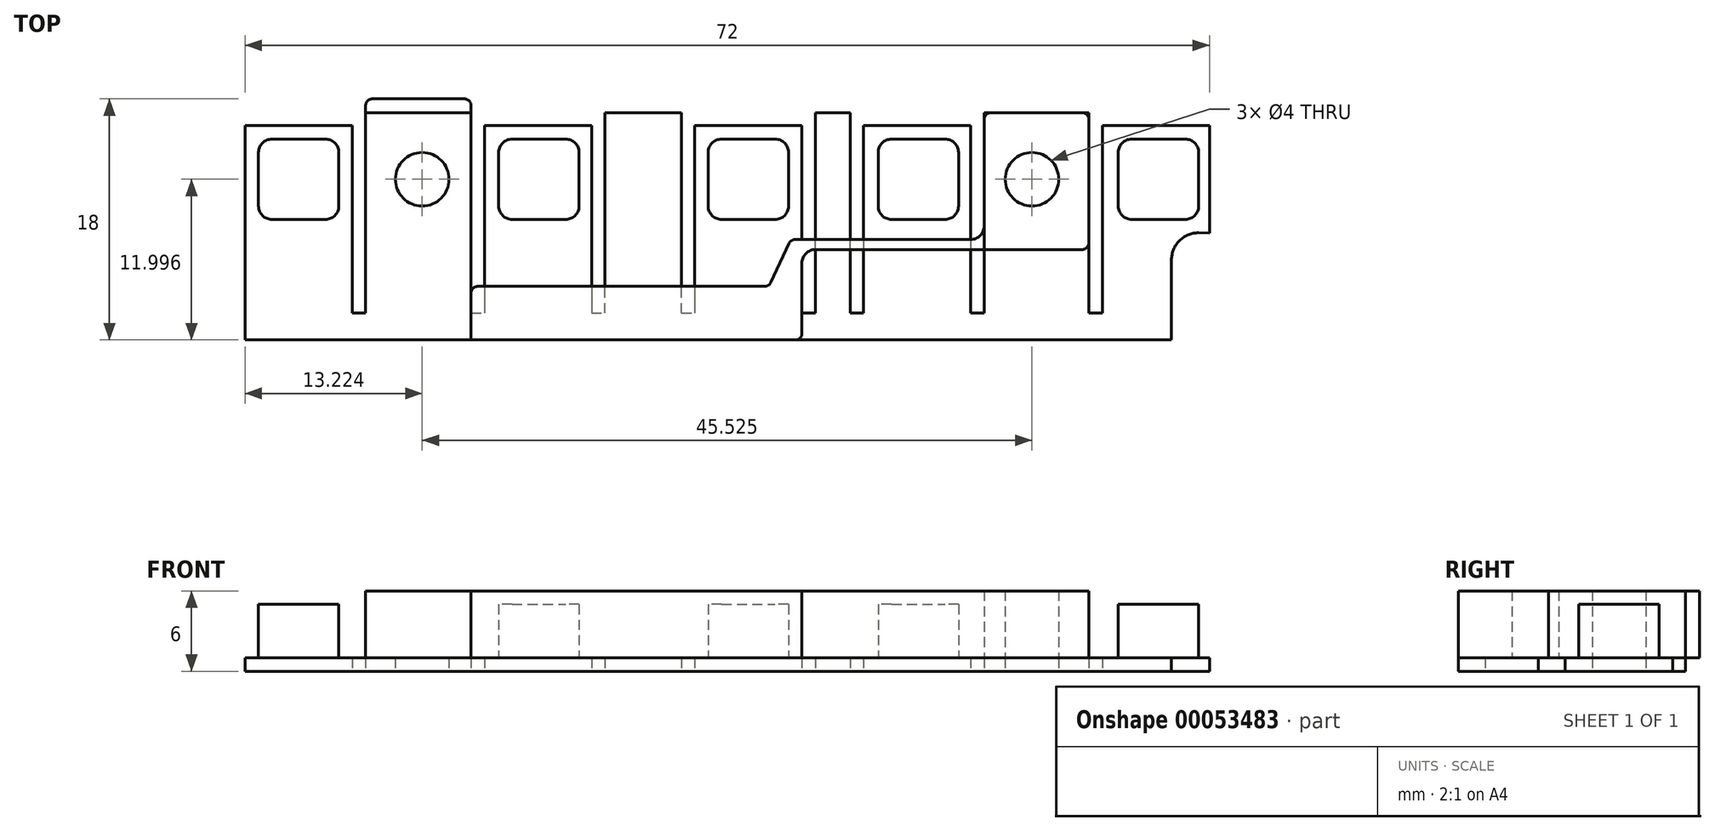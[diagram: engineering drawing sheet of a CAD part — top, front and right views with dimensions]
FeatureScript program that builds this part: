
annotation { "Feature Type Name" : "Feature", "Feature Type Description" : "" }
export const myFeature = defineFeature(function(context is Context, id is Id, definition is map)
    precondition{}
    {
        {
            var Q0;
            Q0=qCreatedBy(makeId("Top.planeOp"),FACE);
            var sketch = newSketch(context, id + "F0", { "sketchPlane" : qUnion([Q0])});
            skLineSegment(sketch, "E0.bottom", {"start": v(-36.4, 9.03) * mm, "end": v(39.6, 9.03) * mm});
            skLineSegment(sketch, "E0.top", {"start": v(-36.4, -6.97) * mm, "end": v(39.6, -6.97) * mm});
            skLineSegment(sketch, "E0.left", {"start": v(-36.4, 9.03) * mm, "end": v(-36.4, -6.97) * mm});
            skLineSegment(sketch, "E0.right", {"start": v(39.6, 9.03) * mm, "end": v(39.6, -6.97) * mm});
            skLineSegment(sketch, "E1", {"start": v(-30.3, 13.5) * mm, "end": v(-30.3, -12.05) * mm, "construction": true});
            skLineSegment(sketch, "E2.1.0.0", {"start": v(-21.08, 13.58) * mm, "end": v(-21.08, -11.98) * mm, "construction": true});
            skLineSegment(sketch, "E2.2.0.0", {"start": v(3.27, 13.5) * mm, "end": v(3.27, -12.05) * mm, "construction": true});
            skLineSegment(sketch, "E2.3.0.0", {"start": v(24.45, 13.5) * mm, "end": v(24.45, -12.05) * mm, "construction": true});
            skLineSegment(sketch, "E2.4.0.0", {"start": v(33.7, 13.5) * mm, "end": v(33.7, -12.05) * mm, "construction": true});
            skLineSegment(sketch, "E2.5.0.0", {"start": v(15.87, 13.5) * mm, "end": v(15.87, -12.05) * mm, "construction": true});
            skLineSegment(sketch, "E2.6.0.0", {"start": v(-12.43, 13.5) * mm, "end": v(-12.43, -12.05) * mm, "construction": true});
            skLineSegment(sketch, "E3", {"start": v(-40.05, 5.03) * mm, "end": v(48.02, 5.03) * mm, "construction": true});
            skCircle(sketch, "E4", {"center": v(-21.08, 5.03) * mm, "radius": 2 * mm});
            skCircle(sketch, "E5", {"center": v(24.45, 5.03) * mm, "radius": 2 * mm});
            skLineSegment(sketch, "E6.rect.bottom", {"start": v(-33.3, 8.03) * mm, "end": v(-27.3, 8.03) * mm});
            skLineSegment(sketch, "E6.rect.top", {"start": v(-33.3, 2.03) * mm, "end": v(-27.3, 2.03) * mm});
            skLineSegment(sketch, "E6.rect.left", {"start": v(-33.3, 8.03) * mm, "end": v(-33.3, 2.03) * mm});
            skLineSegment(sketch, "E6.rect.right", {"start": v(-27.3, 8.03) * mm, "end": v(-27.3, 2.03) * mm});
            skPoint(sketch, "E6.rect.middle", {"position": v(-30.3, 5.03) * mm});
            skLineSegment(sketch, "E7.rect.left", {"start": v(-15.36, 8.03) * mm, "end": v(-15.36, 2.03) * mm});
            skLineSegment(sketch, "E7.rect.bottom", {"start": v(-15.36, 8.03) * mm, "end": v(-9.36, 8.03) * mm});
            skLineSegment(sketch, "E7.rect.right", {"start": v(-9.36, 8.03) * mm, "end": v(-9.36, 2.03) * mm});
            skLineSegment(sketch, "E7.rect.top", {"start": v(-15.36, 2.03) * mm, "end": v(-9.36, 2.03) * mm});
            skLineSegment(sketch, "E8.rect.left", {"start": v(0.27, 8.03) * mm, "end": v(0.27, 2.03) * mm});
            skLineSegment(sketch, "E8.rect.bottom", {"start": v(0.27, 8.03) * mm, "end": v(6.27, 8.03) * mm});
            skLineSegment(sketch, "E8.rect.right", {"start": v(6.27, 8.03) * mm, "end": v(6.27, 2.03) * mm});
            skLineSegment(sketch, "E8.rect.top", {"start": v(0.27, 2.03) * mm, "end": v(6.27, 2.03) * mm});
            skLineSegment(sketch, "E9.rect.left", {"start": v(12.96, 8.03) * mm, "end": v(12.96, 2.03) * mm});
            skLineSegment(sketch, "E9.rect.bottom", {"start": v(12.96, 8.03) * mm, "end": v(18.96, 8.03) * mm});
            skLineSegment(sketch, "E9.rect.right", {"start": v(18.96, 8.03) * mm, "end": v(18.96, 2.03) * mm});
            skLineSegment(sketch, "E9.rect.top", {"start": v(12.96, 2.03) * mm, "end": v(18.96, 2.03) * mm});
            skLineSegment(sketch, "E10.rect.left", {"start": v(30.9, 8.03) * mm, "end": v(30.9, 2.03) * mm});
            skLineSegment(sketch, "E10.rect.bottom", {"start": v(30.9, 8.03) * mm, "end": v(36.9, 8.03) * mm});
            skLineSegment(sketch, "E10.rect.right", {"start": v(36.9, 8.03) * mm, "end": v(36.9, 2.03) * mm});
            skLineSegment(sketch, "E10.rect.top", {"start": v(30.9, 2.03) * mm, "end": v(36.9, 2.03) * mm});
            skLineSegment(sketch, "E11", {"start": v(-41.7, 2.03) * mm, "end": v(44.73, 2.03) * mm, "construction": true});
            skLineSegment(sketch, "E12", {"start": v(-41.7, -4.97) * mm, "end": v(44.73, -4.97) * mm, "construction": true});
            skLineSegment(sketch, "E13.top", {"start": v(-36.4, 11.03) * mm, "end": v(39.58, 11.03) * mm});
            skLineSegment(sketch, "E13.left", {"start": v(-36.4, 9.03) * mm, "end": v(-36.4, 11.03) * mm});
            skLineSegment(sketch, "E13.right", {"start": v(39.58, 8.03) * mm, "end": v(39.58, 11.03) * mm});
            skLineSegment(sketch, "E14.bottom", {"start": v(-34.3, 9.03) * mm, "end": v(-26.3, 9.03) * mm});
            skLineSegment(sketch, "E14.left", {"start": v(-34.3, 9.03) * mm, "end": v(-34.3, -4.97) * mm});
            skLineSegment(sketch, "E14.right", {"start": v(-26.3, 9.03) * mm, "end": v(-26.3, -4.97) * mm});
            skLineSegment(sketch, "E15.bottom", {"start": v(-26.3, -4.97) * mm, "end": v(-36.4, -4.97) * mm});
            skLineSegment(sketch, "E15.right", {"start": v(-36.4, -4.97) * mm, "end": v(-36.4, 9.03) * mm});
            skLineSegment(sketch, "E16.bottom", {"start": v(-35.3, -4.97) * mm, "end": v(-25.3, -4.97) * mm});
            skLineSegment(sketch, "E16.top", {"start": v(-35.3, 9.03) * mm, "end": v(-25.3, 9.03) * mm});
            skLineSegment(sketch, "E16.left", {"start": v(-35.3, -4.97) * mm, "end": v(-35.3, 9.03) * mm});
            skLineSegment(sketch, "E16.right", {"start": v(-25.3, -4.97) * mm, "end": v(-25.3, 9.03) * mm});
            skLineSegment(sketch, "E17.right", {"start": v(-7.43, -4.97) * mm, "end": v(-7.43, 9.03) * mm});
            skLineSegment(sketch, "E17.top", {"start": v(-17.43, 9.03) * mm, "end": v(-7.43, 9.03) * mm});
            skLineSegment(sketch, "E17.left", {"start": v(-17.43, -4.97) * mm, "end": v(-17.43, 9.03) * mm});
            skLineSegment(sketch, "E17.bottom", {"start": v(-17.43, -4.97) * mm, "end": v(-7.43, -4.97) * mm});
            skLineSegment(sketch, "E18.left", {"start": v(-16.43, 9.03) * mm, "end": v(-16.43, -4.97) * mm});
            skLineSegment(sketch, "E18.right", {"start": v(-8.43, 9.03) * mm, "end": v(-8.43, -4.97) * mm});
            skLineSegment(sketch, "E18.bottom", {"start": v(-16.43, 9.03) * mm, "end": v(-8.43, 9.03) * mm});
            skLineSegment(sketch, "E19.right", {"start": v(8.27, -4.97) * mm, "end": v(8.27, 9.03) * mm});
            skLineSegment(sketch, "E19.top", {"start": v(-1.73, 9.03) * mm, "end": v(8.27, 9.03) * mm});
            skLineSegment(sketch, "E19.left", {"start": v(-1.73, -4.97) * mm, "end": v(-1.73, 9.03) * mm});
            skLineSegment(sketch, "E19.bottom", {"start": v(-1.73, -4.97) * mm, "end": v(8.27, -4.97) * mm});
            skLineSegment(sketch, "E20.left", {"start": v(-0.73, 9.03) * mm, "end": v(-0.73, -4.97) * mm});
            skLineSegment(sketch, "E20.right", {"start": v(7.27, 9.03) * mm, "end": v(7.27, -4.97) * mm});
            skLineSegment(sketch, "E20.bottom", {"start": v(-0.73, 9.03) * mm, "end": v(7.27, 9.03) * mm});
            skLineSegment(sketch, "E21.right", {"start": v(20.87, -4.97) * mm, "end": v(20.87, 9.03) * mm});
            skLineSegment(sketch, "E21.top", {"start": v(10.87, 9.03) * mm, "end": v(20.87, 9.03) * mm});
            skLineSegment(sketch, "E21.left", {"start": v(10.87, -4.97) * mm, "end": v(10.87, 9.03) * mm});
            skLineSegment(sketch, "E21.bottom", {"start": v(10.87, -4.97) * mm, "end": v(20.87, -4.97) * mm});
            skLineSegment(sketch, "E22.left", {"start": v(11.87, 9.03) * mm, "end": v(11.87, -4.97) * mm});
            skLineSegment(sketch, "E22.right", {"start": v(19.87, 9.03) * mm, "end": v(19.87, -4.97) * mm});
            skLineSegment(sketch, "E22.bottom", {"start": v(11.87, 9.03) * mm, "end": v(19.87, 9.03) * mm});
            skLineSegment(sketch, "E23.right", {"start": v(38.7, -4.97) * mm, "end": v(38.7, 9.03) * mm});
            skLineSegment(sketch, "E23.top", {"start": v(28.7, 9.03) * mm, "end": v(38.7, 9.03) * mm});
            skLineSegment(sketch, "E23.left", {"start": v(28.7, -4.97) * mm, "end": v(28.7, 9.03) * mm});
            skLineSegment(sketch, "E23.bottom", {"start": v(28.7, -4.97) * mm, "end": v(38.7, -4.97) * mm});
            skLineSegment(sketch, "E24.left", {"start": v(29.7, 9.03) * mm, "end": v(29.7, -4.97) * mm});
            skLineSegment(sketch, "E24.right", {"start": v(37.7, 9.03) * mm, "end": v(37.7, -4.97) * mm});
            skLineSegment(sketch, "E24.bottom", {"start": v(29.7, 9.03) * mm, "end": v(37.7, 9.03) * mm});
            skLineSegment(sketch, "E25.bottom", {"start": v(-36.4, 9.03) * mm, "end": v(39.58, 9.03) * mm});
            skLineSegment(sketch, "E25.top", {"start": v(-36.4, 10) * mm, "end": v(39.58, 10) * mm});
            skLineSegment(sketch, "E25.left", {"start": v(-36.4, 9.03) * mm, "end": v(-36.4, 10) * mm});
            skLineSegment(sketch, "E25.right", {"start": v(39.58, 9.03) * mm, "end": v(39.58, 10) * mm});
            skLineSegment(sketch, "E26.bottom", {"start": v(-35.3, 9.03) * mm, "end": v(-34.23, 9.03) * mm});
            skLineSegment(sketch, "E26.top", {"start": v(-35.3, 10) * mm, "end": v(-34.23, 10) * mm});
            skLineSegment(sketch, "E26.left", {"start": v(-35.3, 9.03) * mm, "end": v(-35.3, 10) * mm});
            skLineSegment(sketch, "E26.right", {"start": v(-34.23, 9.03) * mm, "end": v(-34.23, 10) * mm});
            skLineSegment(sketch, "E27.bottom", {"start": v(-26.3, 9.03) * mm, "end": v(-25.3, 9.03) * mm});
            skLineSegment(sketch, "E27.top", {"start": v(-26.3, 10) * mm, "end": v(-25.3, 10) * mm});
            skLineSegment(sketch, "E27.left", {"start": v(-26.3, 9.03) * mm, "end": v(-26.3, 10) * mm});
            skLineSegment(sketch, "E27.right", {"start": v(-25.3, 9.03) * mm, "end": v(-25.3, 10) * mm});
            skLineSegment(sketch, "E28.bottom", {"start": v(-17.43, 9.03) * mm, "end": v(-16.43, 9.03) * mm});
            skLineSegment(sketch, "E28.top", {"start": v(-17.43, 10) * mm, "end": v(-16.43, 10) * mm});
            skLineSegment(sketch, "E28.left", {"start": v(-17.43, 9.03) * mm, "end": v(-17.43, 10) * mm});
            skLineSegment(sketch, "E28.right", {"start": v(-16.43, 9.03) * mm, "end": v(-16.43, 10) * mm});
            skLineSegment(sketch, "E29.bottom", {"start": v(-8.43, 9.03) * mm, "end": v(-7.43, 9.03) * mm});
            skLineSegment(sketch, "E29.top", {"start": v(-8.43, 10) * mm, "end": v(-7.43, 10) * mm});
            skLineSegment(sketch, "E29.left", {"start": v(-8.43, 9.03) * mm, "end": v(-8.43, 10) * mm});
            skLineSegment(sketch, "E29.right", {"start": v(-7.43, 9.03) * mm, "end": v(-7.43, 10) * mm});
            skLineSegment(sketch, "E30.bottom", {"start": v(-1.73, 9.03) * mm, "end": v(-0.73, 9.03) * mm});
            skLineSegment(sketch, "E30.top", {"start": v(-1.73, 10) * mm, "end": v(-0.73, 10) * mm});
            skLineSegment(sketch, "E30.left", {"start": v(-1.73, 9.03) * mm, "end": v(-1.73, 10) * mm});
            skLineSegment(sketch, "E30.right", {"start": v(-0.73, 9.03) * mm, "end": v(-0.73, 10) * mm});
            skLineSegment(sketch, "E31.bottom", {"start": v(7.27, 9.03) * mm, "end": v(8.27, 9.03) * mm});
            skLineSegment(sketch, "E31.top", {"start": v(7.27, 10) * mm, "end": v(8.27, 10) * mm});
            skLineSegment(sketch, "E31.left", {"start": v(7.27, 9.03) * mm, "end": v(7.27, 10) * mm});
            skLineSegment(sketch, "E31.right", {"start": v(8.27, 9.03) * mm, "end": v(8.27, 10) * mm});
            skLineSegment(sketch, "E32.bottom", {"start": v(10.87, 9.03) * mm, "end": v(11.87, 9.03) * mm});
            skLineSegment(sketch, "E32.top", {"start": v(10.87, 10) * mm, "end": v(11.87, 10) * mm});
            skLineSegment(sketch, "E32.left", {"start": v(10.87, 9.03) * mm, "end": v(10.87, 10) * mm});
            skLineSegment(sketch, "E32.right", {"start": v(11.87, 9.03) * mm, "end": v(11.87, 10) * mm});
            skLineSegment(sketch, "E33.bottom", {"start": v(19.87, 9.03) * mm, "end": v(20.87, 9.03) * mm});
            skLineSegment(sketch, "E33.top", {"start": v(19.87, 10) * mm, "end": v(20.87, 10) * mm});
            skLineSegment(sketch, "E33.left", {"start": v(19.87, 9.03) * mm, "end": v(19.87, 10) * mm});
            skLineSegment(sketch, "E33.right", {"start": v(20.87, 9.03) * mm, "end": v(20.87, 10) * mm});
            skLineSegment(sketch, "E34.bottom", {"start": v(28.7, 9.03) * mm, "end": v(29.7, 9.03) * mm});
            skLineSegment(sketch, "E34.top", {"start": v(28.7, 10) * mm, "end": v(29.7, 10) * mm});
            skLineSegment(sketch, "E34.left", {"start": v(28.7, 9.03) * mm, "end": v(28.7, 10) * mm});
            skLineSegment(sketch, "E34.right", {"start": v(29.7, 9.03) * mm, "end": v(29.7, 10) * mm});
            skLineSegment(sketch, "E35.bottom", {"start": v(37.7, 9.03) * mm, "end": v(38.7, 9.03) * mm});
            skLineSegment(sketch, "E35.top", {"start": v(37.7, 10) * mm, "end": v(38.7, 10) * mm});
            skLineSegment(sketch, "E35.left", {"start": v(37.7, 9.03) * mm, "end": v(37.7, 10) * mm});
            skLineSegment(sketch, "E35.right", {"start": v(38.7, 9.03) * mm, "end": v(38.7, 10) * mm});
            skLineSegment(sketch, "E36", {"start": v(-25.3, 10) * mm, "end": v(-25.3, 11.03) * mm});
            skLineSegment(sketch, "E37", {"start": v(28.7, 10) * mm, "end": v(28.7, 11.03) * mm});
            skLineSegment(sketch, "E38", {"start": v(38.7, -4.97) * mm, "end": v(39.6, -4.97) * mm});
            skCircle(sketch, "E39", {"center": v(36.87, -0.97) * mm, "radius": 2 * mm});
            skLineSegment(sketch, "E40", {"start": v(34.87, -0.95) * mm, "end": v(34.87, -4.97) * mm});
            skLineSegment(sketch, "E41", {"start": v(36.9, 1.03) * mm, "end": v(39.6, 0.99) * mm});
            skLineSegment(sketch, "E42", {"start": v(-34.3, -4.97) * mm, "end": v(-34.3, -6.97) * mm});
            skLineSegment(sketch, "E43", {"start": v(34.87, -4.97) * mm, "end": v(34.87, -6.97) * mm});
            skSolve(sketch);
        }
        {
            var Q0;
            {var subQ4=sQuery(id+"F0.wireOp",EDGE,"E28.top");Q0=makeQuery(id+"F0.imprint","IMPRINT",FACE,{"disambiguationData":[TD([[makeQuery(id+"F0.imprint","IMPRINT",EDGE,{"derivedFrom":subQ4}),1.0]])]});}
            var Q1;
            Q1=makeQuery(id+"F0.imprint","IMPRINT",FACE,{"disambiguationData":[TD([[makeQuery(id+"F0.imprint","IMPRINT",EDGE,{"derivedFrom":sQuery(id+"F0.wireOp",EDGE,"E6.rect.bottom")}),-1.0]])]});
            var Q2;
            Q2=makeQuery(id+"F0.imprint","IMPRINT",FACE,{"disambiguationData":[TD([[makeQuery(id+"F0.imprint","IMPRINT",EDGE,{"derivedFrom":sQuery(id+"F0.wireOp",EDGE,"E6.rect.bottom")}),1.0]])]});
            var Q3;
            Q3=makeQuery(id+"F0.imprint","IMPRINT",FACE,{"disambiguationData":[TD([[makeQuery(id+"F0.imprint","IMPRINT",EDGE,{"derivedFrom":sQuery(id+"F0.wireOp",EDGE,"E7.rect.left")}),1.0]])]});
            var Q4;
            Q4=makeQuery(id+"F0.imprint","IMPRINT",FACE,{"disambiguationData":[TD([[makeQuery(id+"F0.imprint","IMPRINT",EDGE,{"derivedFrom":sQuery(id+"F0.wireOp",EDGE,"E7.rect.left")}),-1.0]])]});
            var Q5;
            Q5=makeQuery(id+"F0.imprint","IMPRINT",FACE,{"disambiguationData":[TD([[makeQuery(id+"F0.imprint","IMPRINT",EDGE,{"derivedFrom":sQuery(id+"F0.wireOp",EDGE,"E8.rect.left")}),1.0]])]});
            var Q6;
            Q6=makeQuery(id+"F0.imprint","IMPRINT",FACE,{"disambiguationData":[TD([[makeQuery(id+"F0.imprint","IMPRINT",EDGE,{"derivedFrom":sQuery(id+"F0.wireOp",EDGE,"E8.rect.left")}),-1.0]])]});
            var Q7;
            Q7=makeQuery(id+"F0.imprint","IMPRINT",FACE,{"disambiguationData":[TD([[makeQuery(id+"F0.imprint","IMPRINT",EDGE,{"derivedFrom":sQuery(id+"F0.wireOp",EDGE,"E9.rect.left")}),1.0]])]});
            var Q8;
            Q8=makeQuery(id+"F0.imprint","IMPRINT",FACE,{"disambiguationData":[TD([[makeQuery(id+"F0.imprint","IMPRINT",EDGE,{"derivedFrom":sQuery(id+"F0.wireOp",EDGE,"E9.rect.left")}),-1.0]])]});
            var Q9;
            Q9=makeQuery(id+"F0.imprint","IMPRINT",FACE,{"disambiguationData":[TD([[makeQuery(id+"F0.imprint","IMPRINT",EDGE,{"derivedFrom":sQuery(id+"F0.wireOp",EDGE,"E10.rect.left")}),1.0]])]});
            var Q10;
            Q10=makeQuery(id+"F0.imprint","IMPRINT",FACE,{"disambiguationData":[TD([[makeQuery(id+"F0.imprint","IMPRINT",EDGE,{"derivedFrom":sQuery(id+"F0.wireOp",EDGE,"E10.rect.left")}),-1.0]])]});
            var Q11;
            {var subQ0=sQuery(id+"F0.wireOp",EDGE,"E27.right");Q11=makeQuery(id+"F0.imprint","IMPRINT",FACE,{"disambiguationData":[TD([[makeQuery(id+"F0.imprint","IMPRINT",EDGE,{"derivedFrom":subQ0}),-1.0]])]});}
            var Q12;
            {var subQ0=sQuery(id+"F0.wireOp",EDGE,"E29.right");Q12=makeQuery(id+"F0.imprint","IMPRINT",FACE,{"disambiguationData":[TD([[makeQuery(id+"F0.imprint","IMPRINT",EDGE,{"derivedFrom":subQ0}),-1.0]])]});}
            var Q13;
            {var subQ0=sQuery(id+"F0.wireOp",EDGE,"E31.right");Q13=makeQuery(id+"F0.imprint","IMPRINT",FACE,{"disambiguationData":[TD([[makeQuery(id+"F0.imprint","IMPRINT",EDGE,{"derivedFrom":subQ0}),-1.0]])]});}
            var Q14;
            {var subQ0=sQuery(id+"F0.wireOp",EDGE,"E33.right");Q14=makeQuery(id+"F0.imprint","IMPRINT",FACE,{"disambiguationData":[TD([[makeQuery(id+"F0.imprint","IMPRINT",EDGE,{"derivedFrom":subQ0}),-1.0]])]});}
            var Q15;
            Q15=makeQuery(id+"F0.imprint","IMPRINT",FACE,{"disambiguationData":[TD([[makeQuery(id+"F0.imprint","IMPRINT",EDGE,{"derivedFrom":sQuery(id+"F0.wireOp",EDGE,"E4")}),-1.0]])]});
            extrude(context, id + "F1", {"entities" : qUnion([Q0, Q1, Q2, Q3, Q4, Q5, Q6, Q7, Q8, Q9, Q10, Q11, Q12, Q13, Q14, Q15]), "depth" : 1 * mm});
        }
        {
            var Q0;
            Q0=makeQuery(id+"F0.imprint","IMPRINT",FACE,{"disambiguationData":[TD([[makeQuery(id+"F0.imprint","IMPRINT",EDGE,{"derivedFrom":sQuery(id+"F0.wireOp",EDGE,"E6.rect.bottom")}),-1.0]])]});
            var Q1;
            Q1=makeQuery(id+"F0.imprint","IMPRINT",FACE,{"disambiguationData":[TD([[makeQuery(id+"F0.imprint","IMPRINT",EDGE,{"derivedFrom":sQuery(id+"F0.wireOp",EDGE,"E7.rect.left")}),1.0]])]});
            var Q2;
            Q2=makeQuery(id+"F0.imprint","IMPRINT",FACE,{"disambiguationData":[TD([[makeQuery(id+"F0.imprint","IMPRINT",EDGE,{"derivedFrom":sQuery(id+"F0.wireOp",EDGE,"E8.rect.left")}),1.0]])]});
            var Q3;
            Q3=makeQuery(id+"F0.imprint","IMPRINT",FACE,{"disambiguationData":[TD([[makeQuery(id+"F0.imprint","IMPRINT",EDGE,{"derivedFrom":sQuery(id+"F0.wireOp",EDGE,"E9.rect.left")}),1.0]])]});
            var Q4;
            Q4=makeQuery(id+"F0.imprint","IMPRINT",FACE,{"disambiguationData":[TD([[makeQuery(id+"F0.imprint","IMPRINT",EDGE,{"derivedFrom":sQuery(id+"F0.wireOp",EDGE,"E10.rect.left")}),1.0]])]});
            extrude(context, id + "F2", {"entities" : qUnion([Q0, Q1, Q2, Q3, Q4]), "operationType" : NewBodyOperationType.ADD, "depth" : 5 * mm});
        }
        {
            var Q0;
            Q0=makeQuery(id+"F2.opExtrude","SWEPT_EDGE",EDGE,{"disambiguationData":[OSD([sQuery(id+"F0.wireOp",EDGE,"E6.rect.top"),sQuery(id+"F0.wireOp",EDGE,"E6.rect.left")])]});
            var Q1;
            Q1=makeQuery(id+"F2.opExtrude","SWEPT_EDGE",EDGE,{"disambiguationData":[OSD([sQuery(id+"F0.wireOp",EDGE,"E6.rect.top"),sQuery(id+"F0.wireOp",EDGE,"E6.rect.right")])]});
            var Q2;
            Q2=makeQuery(id+"F2.opExtrude","SWEPT_EDGE",EDGE,{"disambiguationData":[OSD([sQuery(id+"F0.wireOp",EDGE,"E6.rect.bottom"),sQuery(id+"F0.wireOp",EDGE,"E6.rect.left")])]});
            var Q3;
            Q3=makeQuery(id+"F2.opExtrude","SWEPT_EDGE",EDGE,{"disambiguationData":[OSD([sQuery(id+"F0.wireOp",EDGE,"E7.rect.left"),sQuery(id+"F0.wireOp",EDGE,"E7.rect.top")])]});
            var Q4;
            Q4=makeQuery(id+"F2.opExtrude","SWEPT_EDGE",EDGE,{"disambiguationData":[OSD([sQuery(id+"F0.wireOp",EDGE,"E7.rect.left"),sQuery(id+"F0.wireOp",EDGE,"E7.rect.bottom")])]});
            var Q5;
            Q5=makeQuery(id+"F2.opExtrude","SWEPT_EDGE",EDGE,{"disambiguationData":[OSD([sQuery(id+"F0.wireOp",EDGE,"E7.rect.right"),sQuery(id+"F0.wireOp",EDGE,"E7.rect.top")])]});
            var Q6;
            Q6=makeQuery(id+"F2.opExtrude","SWEPT_EDGE",EDGE,{"disambiguationData":[OSD([sQuery(id+"F0.wireOp",EDGE,"E8.rect.left"),sQuery(id+"F0.wireOp",EDGE,"E8.rect.top")])]});
            var Q7;
            Q7=makeQuery(id+"F2.opExtrude","SWEPT_EDGE",EDGE,{"disambiguationData":[OSD([sQuery(id+"F0.wireOp",EDGE,"E8.rect.left"),sQuery(id+"F0.wireOp",EDGE,"E8.rect.bottom")])]});
            var Q8;
            Q8=makeQuery(id+"F2.opExtrude","SWEPT_EDGE",EDGE,{"disambiguationData":[OSD([sQuery(id+"F0.wireOp",EDGE,"E8.rect.right"),sQuery(id+"F0.wireOp",EDGE,"E8.rect.top")])]});
            var Q9;
            Q9=makeQuery(id+"F2.opExtrude","SWEPT_EDGE",EDGE,{"disambiguationData":[OSD([sQuery(id+"F0.wireOp",EDGE,"E9.rect.left"),sQuery(id+"F0.wireOp",EDGE,"E9.rect.top")])]});
            var Q10;
            Q10=makeQuery(id+"F2.opExtrude","SWEPT_EDGE",EDGE,{"disambiguationData":[OSD([sQuery(id+"F0.wireOp",EDGE,"E9.rect.left"),sQuery(id+"F0.wireOp",EDGE,"E9.rect.bottom")])]});
            var Q11;
            Q11=makeQuery(id+"F2.opExtrude","SWEPT_EDGE",EDGE,{"disambiguationData":[OSD([sQuery(id+"F0.wireOp",EDGE,"E9.rect.right"),sQuery(id+"F0.wireOp",EDGE,"E9.rect.top")])]});
            var Q12;
            Q12=makeQuery(id+"F2.opExtrude","SWEPT_EDGE",EDGE,{"disambiguationData":[OSD([sQuery(id+"F0.wireOp",EDGE,"E10.rect.left"),sQuery(id+"F0.wireOp",EDGE,"E10.rect.top")])]});
            var Q13;
            Q13=makeQuery(id+"F2.opExtrude","SWEPT_EDGE",EDGE,{"disambiguationData":[OSD([sQuery(id+"F0.wireOp",EDGE,"E10.rect.left"),sQuery(id+"F0.wireOp",EDGE,"E10.rect.bottom")])]});
            var Q14;
            Q14=makeQuery(id+"F2.opExtrude","SWEPT_EDGE",EDGE,{"disambiguationData":[OSD([sQuery(id+"F0.wireOp",EDGE,"E10.rect.right"),sQuery(id+"F0.wireOp",EDGE,"E10.rect.top")])]});
            var Q15;
            Q15=makeQuery(id+"F2.opExtrude","SWEPT_EDGE",EDGE,{"disambiguationData":[OSD([sQuery(id+"F0.wireOp",EDGE,"E10.rect.bottom"),sQuery(id+"F0.wireOp",EDGE,"E10.rect.right")])]});
            var Q16;
            Q16=makeQuery(id+"F2.opExtrude","SWEPT_EDGE",EDGE,{"disambiguationData":[OSD([sQuery(id+"F0.wireOp",EDGE,"E9.rect.bottom"),sQuery(id+"F0.wireOp",EDGE,"E9.rect.right")])]});
            var Q17;
            Q17=makeQuery(id+"F2.opExtrude","SWEPT_EDGE",EDGE,{"disambiguationData":[OSD([sQuery(id+"F0.wireOp",EDGE,"E8.rect.bottom"),sQuery(id+"F0.wireOp",EDGE,"E8.rect.right")])]});
            var Q18;
            Q18=makeQuery(id+"F2.opExtrude","SWEPT_EDGE",EDGE,{"disambiguationData":[OSD([sQuery(id+"F0.wireOp",EDGE,"E7.rect.bottom"),sQuery(id+"F0.wireOp",EDGE,"E7.rect.right")])]});
            var Q19;
            Q19=makeQuery(id+"F2.opExtrude","SWEPT_EDGE",EDGE,{"disambiguationData":[OSD([sQuery(id+"F0.wireOp",EDGE,"E6.rect.bottom"),sQuery(id+"F0.wireOp",EDGE,"E6.rect.right")])]});
            fillet(context, id + "F3", {"entities" : qUnion([Q0, Q1, Q2, Q3, Q4, Q5, Q6, Q7, Q8, Q9, Q10, Q11, Q12, Q13, Q14, Q15, Q16, Q17, Q18, Q19]), "radius" : 1 * mm, "tangentPropagation" : true, "allowEdgeOverflow" : false});
        }
        {
            var Q0;
            Q0=makeQuery(id+"F1.opExtrude","CAP_FACE",FACE,{"disambiguationData":[OSD([sQuery(id+"F0.wireOp",EDGE,"E0.top"),sQuery(id+"F0.wireOp",EDGE,"E4"),sQuery(id+"F0.wireOp",EDGE,"E5"),sQuery(id+"F0.wireOp",EDGE,"E13.top"),sQuery(id+"F0.wireOp",EDGE,"E14.left"),sQuery(id+"F0.wireOp",EDGE,"E14.right"),sQuery(id+"F0.wireOp",EDGE,"E16.bottom"),sQuery(id+"F0.wireOp",EDGE,"E16.right"),sQuery(id+"F0.wireOp",EDGE,"E17.right"),sQuery(id+"F0.wireOp",EDGE,"E17.left"),sQuery(id+"F0.wireOp",EDGE,"E17.bottom"),sQuery(id+"F0.wireOp",EDGE,"E18.left"),sQuery(id+"F0.wireOp",EDGE,"E18.right"),sQuery(id+"F0.wireOp",EDGE,"E19.right"),sQuery(id+"F0.wireOp",EDGE,"E19.left"),sQuery(id+"F0.wireOp",EDGE,"E19.bottom"),sQuery(id+"F0.wireOp",EDGE,"E20.left"),sQuery(id+"F0.wireOp",EDGE,"E20.right"),sQuery(id+"F0.wireOp",EDGE,"E21.right"),sQuery(id+"F0.wireOp",EDGE,"E21.left"),sQuery(id+"F0.wireOp",EDGE,"E21.bottom"),sQuery(id+"F0.wireOp",EDGE,"E22.left"),sQuery(id+"F0.wireOp",EDGE,"E22.right"),sQuery(id+"F0.wireOp",EDGE,"E23.left"),sQuery(id+"F0.wireOp",EDGE,"E23.bottom"),sQuery(id+"F0.wireOp",EDGE,"E24.left"),sQuery(id+"F0.wireOp",EDGE,"E24.right"),sQuery(id+"F0.wireOp",EDGE,"E25.bottom"),sQuery(id+"F0.wireOp",EDGE,"E25.top"),sQuery(id+"F0.wireOp",EDGE,"E26.bottom"),sQuery(id+"F0.wireOp",EDGE,"E27.right"),sQuery(id+"F0.wireOp",EDGE,"E28.top"),sQuery(id+"F0.wireOp",EDGE,"E28.left"),sQuery(id+"F0.wireOp",EDGE,"E29.top"),sQuery(id+"F0.wireOp",EDGE,"E29.right"),sQuery(id+"F0.wireOp",EDGE,"E30.top"),sQuery(id+"F0.wireOp",EDGE,"E30.left"),sQuery(id+"F0.wireOp",EDGE,"E31.top"),sQuery(id+"F0.wireOp",EDGE,"E31.right"),sQuery(id+"F0.wireOp",EDGE,"E32.top"),sQuery(id+"F0.wireOp",EDGE,"E32.left"),sQuery(id+"F0.wireOp",EDGE,"E33.top"),sQuery(id+"F0.wireOp",EDGE,"E33.right"),sQuery(id+"F0.wireOp",EDGE,"E34.left"),sQuery(id+"F0.wireOp",EDGE,"E36"),sQuery(id+"F0.wireOp",EDGE,"E37"),sQuery(id+"F0.wireOp",EDGE,"E39"),sQuery(id+"F0.wireOp",EDGE,"E40"),sQuery(id+"F0.wireOp",EDGE,"E41"),sQuery(id+"F0.wireOp",EDGE,"E42"),sQuery(id+"F0.wireOp",EDGE,"E43")])],"isStart":false});
            var sketch = newSketch(context, id + "F4", { "sketchPlane" : qUnion([Q0])});
            skLineSegment(sketch, "E44.bottom", {"start": v(-25.3, 11.03) * mm, "end": v(-17.43, 11.03) * mm});
            skLineSegment(sketch, "E44.top", {"start": v(-25.3, -6.97) * mm, "end": v(-17.43, -6.97) * mm});
            skLineSegment(sketch, "E44.left", {"start": v(-25.3, 11.03) * mm, "end": v(-25.3, -6.97) * mm});
            skLineSegment(sketch, "E44.right", {"start": v(-17.43, 11.03) * mm, "end": v(-17.43, -6.97) * mm});
            skLineSegment(sketch, "E45.right", {"start": v(20.55, -0.22) * mm, "end": v(20.87, -0.22) * mm});
            skLineSegment(sketch, "E46", {"start": v(-21.08, 5.03) * mm, "end": v(24.45, 5.03) * mm, "construction": true});
            skLineSegment(sketch, "E47.bottom", {"start": v(-25.3, -6.97) * mm, "end": v(7.27, -6.97) * mm});
            skLineSegment(sketch, "E47.top", {"start": v(-25.3, -2.97) * mm, "end": v(7.27, -2.97) * mm});
            skLineSegment(sketch, "E47.left", {"start": v(-25.3, -6.97) * mm, "end": v(-25.3, -2.97) * mm});
            skLineSegment(sketch, "E47.right", {"start": v(7.27, -6.97) * mm, "end": v(7.27, -2.97) * mm});
            skLineSegment(sketch, "E48.bottom", {"start": v(7.27, -0.22) * mm, "end": v(20.87, -0.22) * mm});
            skLineSegment(sketch, "E48.top", {"start": v(7.27, 0.53) * mm, "end": v(20.87, 0.53) * mm});
            skLineSegment(sketch, "E48.left", {"start": v(7.27, -0.22) * mm, "end": v(7.27, 0.53) * mm});
            skLineSegment(sketch, "E48.right", {"start": v(20.87, -0.22) * mm, "end": v(20.87, 0.53) * mm});
            skLineSegment(sketch, "E49", {"start": v(7.27, 0.53) * mm, "end": v(6.44, 0.53) * mm});
            skLineSegment(sketch, "E50", {"start": v(6.44, 0.53) * mm, "end": v(4.82, -2.97) * mm});
            skLineSegment(sketch, "E51", {"start": v(4.82, -2.97) * mm, "end": v(7.27, -2.97) * mm});
            skLineSegment(sketch, "E52.bottom", {"start": v(20.87, -0.22) * mm, "end": v(28.7, -0.22) * mm});
            skLineSegment(sketch, "E52.top", {"start": v(20.87, 11.03) * mm, "end": v(28.7, 11.03) * mm});
            skLineSegment(sketch, "E52.left", {"start": v(20.87, -0.22) * mm, "end": v(20.87, 11.03) * mm});
            skLineSegment(sketch, "E52.right", {"start": v(28.7, -0.22) * mm, "end": v(28.7, 11.03) * mm});
            skSolve(sketch);
        }
        {
            var Q0;
            {var subQ3=sQuery(id+"F4.wireOp",EDGE,"E44.right");var subQ6=sQuery(id+"F4.wireOp",EDGE,"E47.bottom");var subQ8=makeQuery(id+"F4.imprint","INTERSECT",VERTEX,{"derivedFrom":[subQ3,subQ6]});Q0=makeQuery(id+"F4.imprint","IMPRINT",FACE,{"disambiguationData":[TD([[makeQuery(id+"F4.imprint","IMPRINT",EDGE,{"disambiguationData":[TD([[subQ8,1.0]])],"derivedFrom":subQ6}),1.0]])]});}
            var Q1;
            {var subQ5=sQuery(id+"F4.wireOp",EDGE,"E45.bottom");Q1=makeQuery(id+"F4.imprint","IMPRINT",FACE,{"disambiguationData":[TD([[makeQuery(id+"F4.imprint","IMPRINT",EDGE,{"derivedFrom":subQ5}),-1.0]])]});}
            var Q2;
            {var subQ1=sQuery(id+"F0.wireOp",EDGE,"E17.bottom");var subQ3=makeQuery(id+"F1.opExtrude","CAP_EDGE",EDGE,{"disambiguationData":[OSD([subQ1]),TDD([makeQuery(id+"F0.imprint","IMPRINT",EDGE,{"disambiguationData":[TD([[makeQuery(id+"F0.imprint","INTERSECT",VERTEX,{"derivedFrom":[sQuery(id+"F0.wireOp",EDGE,"E17.left"),subQ1]}),-1.0]])],"derivedFrom":subQ1})])],"isStart":false});Q2=makeQuery(id+"F4.imprint","IMPRINT",FACE,{"disambiguationData":[TD([[makeQuery(id+"F4.imprint","IMPRINT",EDGE,{"derivedFrom":subQ3}),1.0]])]});}
            var Q3;
            {var subQ0=sQuery(id+"F4.wireOp",EDGE,"E48.left");var subQ1=makeQuery(id+"F4.imprint","INTERSECT",VERTEX,{"derivedFrom":[sQuery(id+"F4.wireOp",EDGE,"E47.top"),subQ0]});Q3=makeQuery(id+"F4.imprint","IMPRINT",FACE,{"disambiguationData":[TD([[makeQuery(id+"F4.imprint","IMPRINT",EDGE,{"disambiguationData":[TD([[subQ1,1.0]])],"derivedFrom":subQ0}),1.0]])]});}
            var Q4;
            {var subQ4=sQuery(id+"F4.wireOp",EDGE,"E48.bottom");var subQ6=makeQuery(id+"F1.opExtrude","CAP_EDGE",EDGE,{"disambiguationData":[OSD([sQuery(id+"F0.wireOp",EDGE,"E22.right")])],"isStart":false});var subQ8=makeQuery(id+"F4.imprint","INTERSECT",VERTEX,{"derivedFrom":[subQ6,subQ4]});Q4=makeQuery(id+"F4.imprint","IMPRINT",FACE,{"disambiguationData":[TD([[makeQuery(id+"F4.imprint","IMPRINT",EDGE,{"disambiguationData":[TD([[subQ8,1.0]])],"derivedFrom":subQ6}),1.0]])]});}
            var Q5;
            {var subQ4=sQuery(id+"F0.wireOp",EDGE,"E17.right");var subQ7=sQuery(id+"F0.wireOp",EDGE,"E17.bottom");var subQ8=makeQuery(id+"F1.opExtrude","CAP_EDGE",EDGE,{"disambiguationData":[OSD([subQ7]),TDD([makeQuery(id+"F0.imprint","IMPRINT",EDGE,{"disambiguationData":[TD([[makeQuery(id+"F0.imprint","INTERSECT",VERTEX,{"derivedFrom":[subQ4,subQ7]}),1.0]])],"derivedFrom":subQ7})])],"isStart":false});Q5=makeQuery(id+"F4.imprint","IMPRINT",FACE,{"disambiguationData":[TD([[makeQuery(id+"F4.imprint","IMPRINT",EDGE,{"derivedFrom":subQ8}),1.0]])]});}
            var Q6;
            {var subQ1=sQuery(id+"F0.wireOp",EDGE,"E19.left");var subQ7=sQuery(id+"F0.wireOp",EDGE,"E19.bottom");var subQ8=makeQuery(id+"F1.opExtrude","CAP_EDGE",EDGE,{"disambiguationData":[OSD([subQ7]),TDD([makeQuery(id+"F0.imprint","IMPRINT",EDGE,{"disambiguationData":[TD([[makeQuery(id+"F0.imprint","INTERSECT",VERTEX,{"derivedFrom":[subQ1,subQ7]}),-1.0]])],"derivedFrom":subQ7})])],"isStart":false});Q6=makeQuery(id+"F4.imprint","IMPRINT",FACE,{"disambiguationData":[TD([[makeQuery(id+"F4.imprint","IMPRINT",EDGE,{"derivedFrom":subQ8}),1.0]])]});}
            var Q7;
            {var subQ0=sQuery(id+"F4.wireOp",EDGE,"E48.bottom");var subQ1=makeQuery(id+"F1.opExtrude","CAP_EDGE",EDGE,{"disambiguationData":[OSD([sQuery(id+"F0.wireOp",EDGE,"E19.right"),sQuery(id+"F0.wireOp",EDGE,"E31.right")])],"isStart":false});var subQ2=makeQuery(id+"F4.imprint","INTERSECT",VERTEX,{"derivedFrom":[subQ1,subQ0]});Q7=makeQuery(id+"F4.imprint","IMPRINT",FACE,{"disambiguationData":[TD([[makeQuery(id+"F4.imprint","IMPRINT",EDGE,{"disambiguationData":[TD([[subQ2,-1.0]])],"derivedFrom":subQ0}),1.0]])]});}
            var Q8;
            {var subQ0=sQuery(id+"F4.wireOp",EDGE,"E48.bottom");var subQ3=makeQuery(id+"F1.opExtrude","CAP_EDGE",EDGE,{"disambiguationData":[OSD([sQuery(id+"F0.wireOp",EDGE,"E22.left")])],"isStart":false});var subQ4=makeQuery(id+"F4.imprint","INTERSECT",VERTEX,{"derivedFrom":[subQ3,subQ0]});Q8=makeQuery(id+"F4.imprint","IMPRINT",FACE,{"disambiguationData":[TD([[makeQuery(id+"F4.imprint","IMPRINT",EDGE,{"disambiguationData":[TD([[subQ4,1.0]])],"derivedFrom":subQ3}),-1.0]])]});}
            var Q9;
            {var subQ0=sQuery(id+"F4.wireOp",EDGE,"E48.bottom");var subQ1=makeQuery(id+"F1.opExtrude","CAP_EDGE",EDGE,{"disambiguationData":[OSD([sQuery(id+"F0.wireOp",EDGE,"E22.left")])],"isStart":false});var subQ2=makeQuery(id+"F4.imprint","INTERSECT",VERTEX,{"derivedFrom":[subQ1,subQ0]});Q9=makeQuery(id+"F4.imprint","IMPRINT",FACE,{"disambiguationData":[TD([[makeQuery(id+"F4.imprint","IMPRINT",EDGE,{"disambiguationData":[TD([[subQ2,-1.0]])],"derivedFrom":subQ0}),1.0]])]});}
            var Q10;
            {var subQ0=sQuery(id+"F0.wireOp",EDGE,"E17.bottom");var subQ2=makeQuery(id+"F1.opExtrude","CAP_EDGE",EDGE,{"disambiguationData":[OSD([subQ0]),TDD([makeQuery(id+"F0.imprint","IMPRINT",EDGE,{"disambiguationData":[TD([[makeQuery(id+"F0.imprint","INTERSECT",VERTEX,{"derivedFrom":[sQuery(id+"F0.wireOp",EDGE,"E17.left"),subQ0]}),-1.0]])],"derivedFrom":subQ0})])],"isStart":false});Q10=makeQuery(id+"F4.imprint","IMPRINT",FACE,{"disambiguationData":[TD([[makeQuery(id+"F4.imprint","IMPRINT",EDGE,{"derivedFrom":subQ2}),-1.0]])]});}
            var Q11;
            {var subQ2=sQuery(id+"F4.wireOp",EDGE,"E44.bottom");Q11=makeQuery(id+"F4.imprint","IMPRINT",FACE,{"disambiguationData":[TD([[makeQuery(id+"F4.imprint","IMPRINT",EDGE,{"derivedFrom":subQ2}),-1.0]])]});}
            var Q12;
            {var subQ1=sQuery(id+"F4.wireOp",EDGE,"E48.left");Q12=makeQuery(id+"F4.imprint","IMPRINT",FACE,{"disambiguationData":[TD([[makeQuery(id+"F4.imprint","IMPRINT",EDGE,{"derivedFrom":subQ1}),-1.0]])]});}
            var Q13;
            {var subQ3=sQuery(id+"F4.wireOp",EDGE,"E52.bottom");Q13=makeQuery(id+"F4.imprint","IMPRINT",FACE,{"disambiguationData":[TD([[makeQuery(id+"F4.imprint","IMPRINT",EDGE,{"derivedFrom":subQ3}),1.0]])]});}
            extrude(context, id + "F5", {"entities" : qUnion([Q0, Q1, Q2, Q3, Q4, Q5, Q6, Q7, Q8, Q9, Q10, Q11, Q12, Q13]), "depth" : 5 * mm});
        }
        {
            var Q0;
            Q0=makeQuery(id+"F5.opExtrude","SWEPT_EDGE",EDGE,{"disambiguationData":[OSD([sQuery(id+"F4.wireOp",EDGE,"E45.right"),sQuery(id+"F4.wireOp",EDGE,"E48.top"),sQuery(id+"F4.wireOp",EDGE,"E48.right")])]});
            var Q1;
            Q1=makeQuery(id+"F5.opExtrude","SWEPT_EDGE",EDGE,{"disambiguationData":[OSD([sQuery(id+"F4.wireOp",EDGE,"E47.right"),sQuery(id+"F4.wireOp",EDGE,"E48.bottom"),sQuery(id+"F4.wireOp",EDGE,"E48.left")])]});
            var Q2;
            Q2=makeQuery(id+"F5.opExtrude","SWEPT_EDGE",EDGE,{"disambiguationData":[OSD([sQuery(id+"F4.wireOp",EDGE,"E45.top"),sQuery(id+"F4.wireOp",EDGE,"E48.right")])]});
            var Q3;
            Q3=makeQuery(id+"F5.opExtrude","SWEPT_EDGE",EDGE,{"disambiguationData":[OSD([sQuery(id+"F0.wireOp",EDGE,"E20.right"),sQuery(id+"F4.wireOp",EDGE,"E48.top"),sQuery(id+"F4.wireOp",EDGE,"E48.left")])]});
            fillet(context, id + "F6", {"entities" : qUnion([Q0, Q1, Q2, Q3]), "radius" : 1 * mm, "tangentPropagation" : true, "allowEdgeOverflow" : false});
        }
        {
            var Q0;
            Q0=makeQuery(id+"F5.opExtrude","SWEPT_EDGE",EDGE,{"disambiguationData":[OSD([sQuery(id+"F4.wireOp",EDGE,"E49"),sQuery(id+"F4.wireOp",EDGE,"E50")])]});
            var Q1;
            Q1=makeQuery(id+"F5.opExtrude","SWEPT_EDGE",EDGE,{"disambiguationData":[OSD([sQuery(id+"F4.wireOp",EDGE,"E47.top"),sQuery(id+"F4.wireOp",EDGE,"E50"),sQuery(id+"F4.wireOp",EDGE,"E51")])]});
            var Q2;
            Q2=makeQuery(id+"F5.opExtrude","SWEPT_EDGE",EDGE,{"disambiguationData":[OSD([sQuery(id+"F0.wireOp",EDGE,"E0.top"),sQuery(id+"F4.wireOp",EDGE,"E47.bottom"),sQuery(id+"F4.wireOp",EDGE,"E47.right")])]});
            var Q3;
            Q3=makeQuery(id+"F5.opExtrude","SWEPT_EDGE",EDGE,{"disambiguationData":[OSD([sQuery(id+"F0.wireOp",EDGE,"E23.left"),sQuery(id+"F0.wireOp",EDGE,"E34.left"),sQuery(id+"F0.wireOp",EDGE,"E37"),sQuery(id+"F4.wireOp",EDGE,"E52.bottom"),sQuery(id+"F4.wireOp",EDGE,"E52.right")])]});
            var Q4;
            Q4=makeQuery(id+"F5.opExtrude","SWEPT_EDGE",EDGE,{"disambiguationData":[OSD([sQuery(id+"F4.wireOp",EDGE,"E52.top"),sQuery(id+"F4.wireOp",EDGE,"E52.right")])]});
            var Q5;
            Q5=makeQuery(id+"F5.opExtrude","SWEPT_EDGE",EDGE,{"disambiguationData":[OSD([sQuery(id+"F0.wireOp",EDGE,"E13.top"),sQuery(id+"F4.wireOp",EDGE,"E52.top"),sQuery(id+"F4.wireOp",EDGE,"E52.left")])]});
            var Q6;
            Q6=makeQuery(id+"F5.opExtrude","SWEPT_EDGE",EDGE,{"disambiguationData":[OSD([sQuery(id+"F4.wireOp",EDGE,"E44.bottom"),sQuery(id+"F4.wireOp",EDGE,"E44.left")])]});
            var Q7;
            Q7=makeQuery(id+"F5.opExtrude","SWEPT_EDGE",EDGE,{"disambiguationData":[OSD([sQuery(id+"F4.wireOp",EDGE,"E44.right"),sQuery(id+"F4.wireOp",EDGE,"E47.top")])]});
            var Q8;
            Q8=makeQuery(id+"F5.opExtrude","SWEPT_EDGE",EDGE,{"disambiguationData":[OSD([sQuery(id+"F0.wireOp",EDGE,"E13.top"),sQuery(id+"F4.wireOp",EDGE,"E44.bottom"),sQuery(id+"F4.wireOp",EDGE,"E44.right")])]});
            var Q9;
            Q9=makeQuery(id+"F5.opExtrude","SWEPT_EDGE",EDGE,{"disambiguationData":[OSD([sQuery(id+"F0.wireOp",EDGE,"E0.top"),sQuery(id+"F4.wireOp",EDGE,"E47.bottom"),sQuery(id+"F4.wireOp",EDGE,"E47.left")])]});
            fillet(context, id + "F7", {"entities" : qUnion([Q0, Q1, Q2, Q3, Q4, Q5, Q6, Q7, Q8, Q9]), "radius" : .5 * mm, "tangentPropagation" : true, "allowEdgeOverflow" : false});
        }
    });
